# Revit family: 55-SANITARIO AQUAPRO RD BLCO
name_source: partatom
category: Aparatos sanitarios
revit_build: Autodesk Revit 2018 (Build: 20170223_1515(x64)
units: mm (PartAtom-declared; Revit-internal decimal feet)

## family parameters
Anfitrión = Muro
Compartido = No
Corte con vacíos al cargar = No
Cota de conector redondo = Diámetro de uso
Número OmniClass = 23.45.55.00
Punto de cálculo de habitación = No
Siempre vertical = Sí
Tipo de pieza = Normal
Título OmniClass = Sanitary Faucets, Wastes

## types (1)
- Tipo 1
    Acabado = Brillante
    Alto Nominal = 785 mm
    Ancho Nominal = 378 mm  [stored 1.24016 ft]
    Característica = Tecnología Maxi Clean, taza sin anillo para mejor lavado, reduce aparición de gérmenes y bacterias, pefil de taza redonda, ahorro de agua
    Color = Blanco
    Consumo de Agua = Promedio 3,8 Lpf. - 1,0gpf.
    Cumplimiento de Norma = Consumo de agua 4,8 y 3,2 l/min. Por descarga. Este producto aplica para obtener certificaciones / puntajes en: LEED, CASA COLOMBIA y EDGE
    Código de montaje = D2030
    Descripción = Sanitary Waste
    Descripción IFC = Aquapro RD Sanitario de dos piezas
    Descripción de la garantía = Porcelana sanitaria garantía de por vida, garantía de 5 años para grifería
    Diámetro de conexión de entrada = 12,7 mm / 1/2"
    Diámetro de conexión sanitaria = 101.6 mm / 4"
    Duración Garantía Partes = Integral de por vida
    Duración Garantía Unidad = Años
    Fabricante = www.corona.com.co
    Forma = Rectangular
    Imagen de tipo = <Ninguno>
    Informacion del producto = https://corona.co
    Longitud Nominal = 666 mm  [stored 2.18504 ft]
    Material = Ceramica_Corona_Blanco
    Material Secundario = Plastico_Corona_Blanco
    Nombre = Sanitario Aquapro
    Numero de Modelo = 278431001
    Presión máxima = 80 PSI
    Presión mínima = 20 PSI
    Requerimientos de Accesibilidad = Manual
    Responsable Garantia Partes = www.corona.com.co
    Tamaño = 666 x 378 x 785
    Tipo de Activo = Fijo
    Tráfico = Residencial

note: [stored X ft] marks values corroborated as IEEE doubles in the binary element streams (Revit-internal decimal feet)
